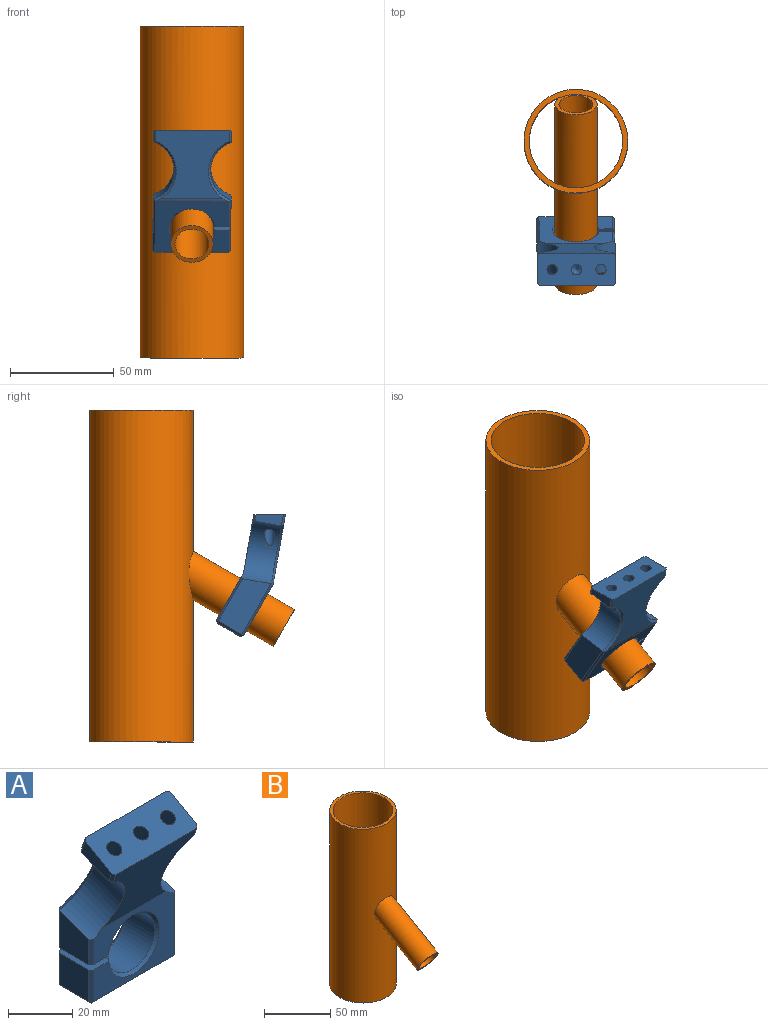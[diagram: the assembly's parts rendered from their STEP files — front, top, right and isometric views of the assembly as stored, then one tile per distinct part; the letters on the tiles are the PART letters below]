
ASSEMBLY  parts=2 mates=2
PART A: 47 faces, bbox 38.1x25.2x61.6 mm
  f0: cylinder r=15mm len=31.65mm, axis (0,0.94,0.34), area 482.8mm2, adj f3,f9,f10,f12,f20,f30,f36,f37
  f1: cylinder r=15mm len=31.65mm, axis (0,0.94,0.34), area 482.7mm2, adj f4,f9,f10,f13,f21,f22,f23,f39
  f2: plane 35.5x31.14mm, normal (0,0.94,0.34), area 752.1mm2, adj f8,f23,f24,f37,f38,f42
  f3: plane 13.33x9.67mm, normal (1,0,0), area 57.4mm2, adj f0,f8,f20,f38
  f4: plane 13.33x9.67mm, normal (-1,0,0), area 57.4mm2, adj f1,f8,f21,f24
  f5: plane 13x12mm, normal (-1,0,0), area 156mm2, adj f14,f25,f26,f28
  f6: plane 35.5x27.76mm, normal (0,1,0), area 575mm2, adj f14,f15,f22,f28,f33,f36,f41,f42
  f7: cylinder r=10.25mm len=20.5mm, axis (0,-1,0), area 811.2mm2, adj f14,f15,f40,f41
  f8: plane 37.5x13.19mm, normal (0,-0.5,0.87), area 510.2mm2, adj f2,f3,f4,f9,f20,f21,f24,f38
  f9: plane 35.5x27mm, normal (0,-0.94,-0.34), area 672.4mm2, adj f0,f1,f8,f10,f20,f21
  f10: plane 35.5x26mm, normal (0,-1,0), area 502.7mm2, adj f0,f1,f9,f14,f15,f25,f29,f30
  f11: plane 35.5x13mm, normal (0,0,-1), area 371.6mm2, adj f16,f26,f29,f33,f34
  f12: plane 28.28x13mm, normal (1,0,0), area 336.9mm2, adj f0,f30,f34,f36
  f13: plane 14.28x13mm, normal (-1,0,0), area 154.9mm2, adj f1,f15,f22,f39
  f14: plane 15x8.55mm, normal (0,0,1), area 106.6mm2, adj f5,f6,f7,f10,f17,f25,f28,f40
  f15: plane 15x8.55mm, normal (0,0,-1), area 112.4mm2, adj f6,f7,f10,f13,f19,f22,f39,f40
  f16: cone r=2.5mm half-angle=45deg, axis (0,0,-1), area 105.3mm2, adj f11,f17,f26
  f17: cylinder r=2.5mm len=9.9mm, axis (0,0,-1), area 155.5mm2, adj f14,f16
  f18: cone r=0mm half-angle=59deg, axis (0,0,-1), area 16.2mm2, adj f19
  f19: cylinder r=2.1mm len=12.4mm, axis (0,0,-1), area 163.6mm2, adj f15,f18
  f20: plane 3.79x2mm, normal (0.71,-0.66,-0.24), area 4.8mm2, adj f0,f3,f8,f9
  f21: plane 3.79x2mm, normal (-0.71,-0.66,-0.24), area 4.8mm2, adj f1,f4,f8,f9
  f22: plane 14.34x1.02mm, normal (-0.71,0.71,0), area 20.1mm2, adj f1,f6,f13,f15,f23,f42
  f23: cone r=15mm half-angle=45deg, axis (0,0.94,0.34), area 52.4mm2, adj f1,f2,f22,f24,f42
  f24: plane 5.75x2.62mm, normal (-0.71,0.66,0.24), area 7.5mm2, adj f2,f4,f8,f23
  f25: plane 12x1mm, normal (-0.71,-0.71,0), area 17mm2, adj f5,f10,f14,f27
  f26: plane 13x1mm, normal (-0.71,0,-0.71), area 12.5mm2, adj f5,f11,f16,f27,f31
  f27: plane 1x1mm, normal (-0.58,-0.58,-0.58), area 0.9mm2, adj f25,f26,f29
  f28: plane 12x1mm, normal (-0.71,0.71,0), area 17mm2, adj f5,f6,f14,f31
  f29: plane 35.5x1mm, normal (0,-0.71,-0.71), area 50.2mm2, adj f10,f11,f27,f32
  f30: plane 23.62x1.01mm, normal (0.71,-0.71,0), area 33.3mm2, adj f0,f10,f12,f32
  f31: plane 1x1mm, normal (-0.58,0.58,-0.58), area 0.9mm2, adj f26,f28,f33
  f32: plane 1x1mm, normal (0.58,-0.58,-0.58), area 0.9mm2, adj f29,f30,f34
  f33: plane 35.5x1mm, normal (0,0.71,-0.71), area 50.2mm2, adj f6,f11,f31,f35
  f34: plane 13x1mm, normal (0.71,0,-0.71), area 18.4mm2, adj f11,f12,f32,f35
  f35: plane 1x1mm, normal (0.58,0.58,-0.58), area 0.9mm2, adj f33,f34,f36
  f36: plane 28.34x1.02mm, normal (0.71,0.71,0), area 39.9mm2, adj f0,f6,f12,f35,f37,f42
  f37: cone r=15mm half-angle=45deg, axis (0,0.94,0.34), area 52.4mm2, adj f0,f2,f36,f38,f42
  f38: plane 5.75x2.62mm, normal (0.71,0.66,0.24), area 7.5mm2, adj f2,f3,f8,f37
  f39: plane 9.62x1.01mm, normal (-0.71,-0.71,0), area 13.5mm2, adj f1,f10,f13,f15
  f40: cone r=10.25mm half-angle=45deg, axis (0,-1,0), area 92.7mm2, adj f7,f10,f14,f15
  f41: cone r=10.25mm half-angle=45deg, axis (0,1,0), area 92.7mm2, adj f6,f7,f14,f15
  f42: cylinder r=5mm len=35.53mm, axis (-1,0,0), area 57.9mm2, adj f2,f6,f22,f23,f36,f37
  f43: cylinder r=2.5mm len=15.45mm, axis (0,-0.5,0.87), area 161.8mm2, adj f1,f8
  f44: cone r=0mm half-angle=59deg, axis (0,-0.5,0.87), area 22.9mm2, adj f45
  f45: cylinder r=2.5mm len=18.09mm, axis (0,-0.5,0.87), area 282.7mm2, adj f8,f44
  f46: cylinder r=2.5mm len=15.45mm, axis (0,-0.5,0.87), area 161.8mm2, adj f0,f8
PART B: 12 faces, bbox 50x98.8x160 mm
  f0: cylinder r=22.5mm len=160mm, axis (0,0,-1), area 22216.4mm2, adj f2,f3,f8,f10
  f1: cylinder r=25mm len=160mm, axis (0,0,-1), area 24746mm2, adj f2,f3,f5
  f2: plane 50x50mm, normal (0,0,1), area 373.1mm2, adj f0,f1
  f3: plane 50x50mm, normal (0,0,-1), area 373.1mm2, adj f0,f1
  f4: plane 20.4x17.67mm, normal (0,-0.87,-0.5), area 115.6mm2, adj f5,f6
  f5: cylinder r=10.2mm len=58.98mm, axis (0,-0.87,-0.5), area 3311.8mm2, adj f1,f4
  f6: cylinder r=8.2mm len=55.98mm, axis (0,-0.87,-0.5), area 2639.1mm2, adj f4,f7
  f7: cylinder r=25mm len=18.94mm, axis (0,0,-1), area 247.3mm2, adj f6
  f8: plane 20.4x16.75mm, normal (0,0.87,0.5), area 102mm2, adj f0,f9,f10
  f9: cylinder r=8.2mm len=52.73mm, axis (0,-0.87,-0.5), area 2359.5mm2, adj f8,f11
  f10: cylinder r=10.2mm len=55.73mm, axis (0,-0.87,-0.5), area 2894.1mm2, adj f0,f8
  f11: cylinder r=22.5mm len=18.94mm, axis (0,0,-1), area 248.1mm2, adj f9
PLACE A rot(axis=(0,0.26,-0.97),179.9deg) t=(-23.73,-50.72,-46.74)mm
PLACE B t=(-23.73,-8.03,-36.69)mm
MATE cylindrical A.f40 <-> B.f5  axis (0,0.87,0.5) through (-23.73,-51.59,-47.24)mm
MATE planar A.f6 <-> B.f5  axis (0,-0.87,-0.5) through (-5.93,-67.6,-47.51)mm
